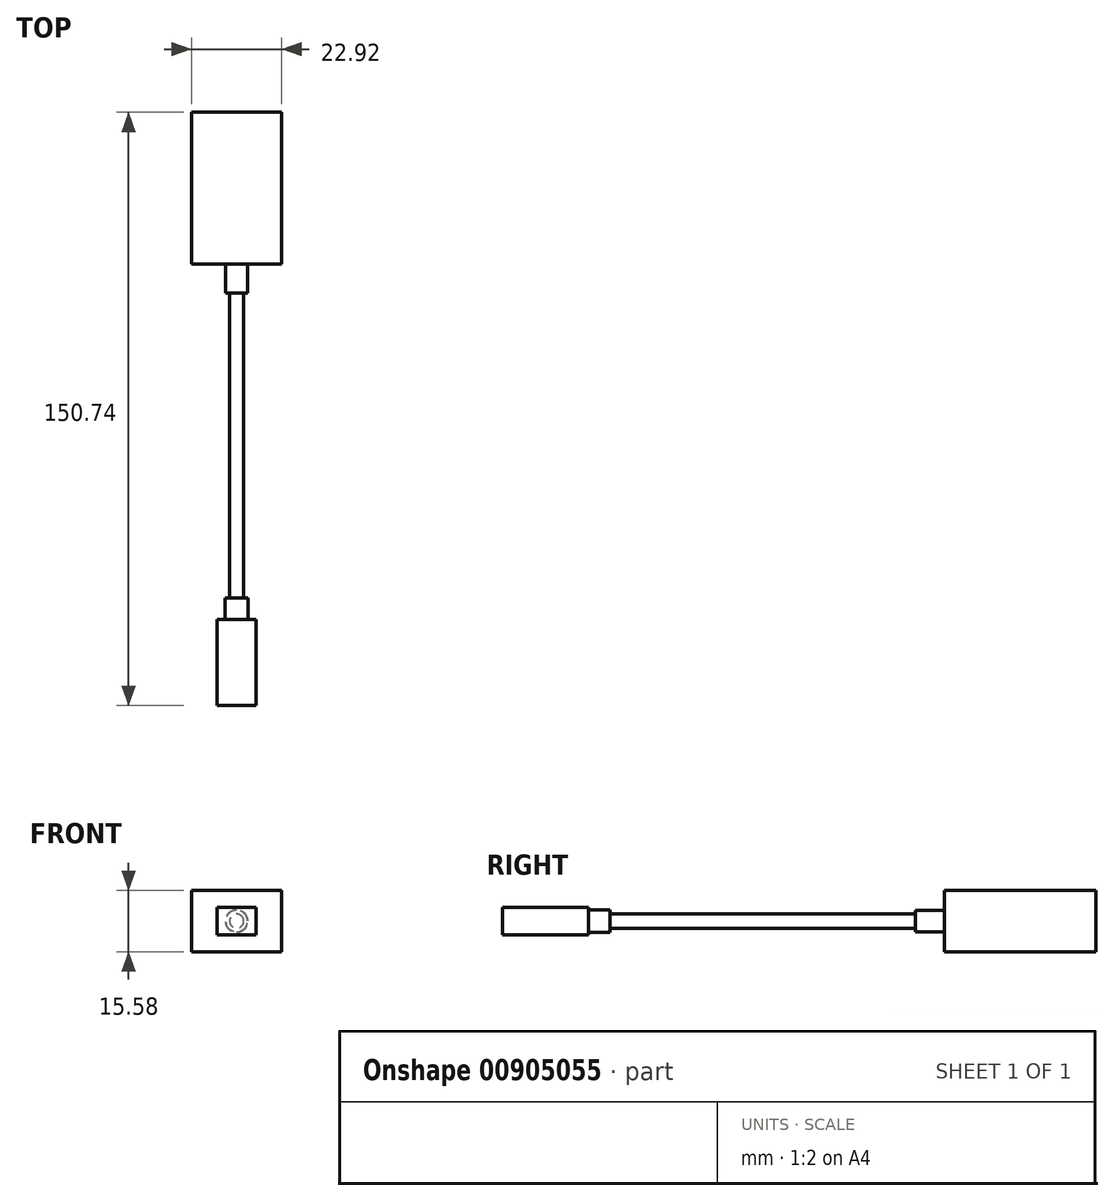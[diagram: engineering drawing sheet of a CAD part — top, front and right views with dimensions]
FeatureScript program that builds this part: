
annotation { "Feature Type Name" : "Feature", "Feature Type Description" : "" }
export const myFeature = defineFeature(function(context is Context, id is Id, definition is map)
    precondition{}
    {
        {
            var Q0;
            Q0=qCreatedBy(makeId("Top.planeOp"),FACE);
            var sketch = newSketch(context, id + "F0", { "sketchPlane" : qUnion([Q0])});
            skLineSegment(sketch, "E0.bottom", {"start": v(4.94, -10.92) * mm, "end": v(-4.94, -10.92) * mm});
            skLineSegment(sketch, "E0.top", {"start": v(4.94, 10.92) * mm, "end": v(-4.94, 10.92) * mm});
            skLineSegment(sketch, "E0.left", {"start": v(4.94, -10.92) * mm, "end": v(4.94, 10.92) * mm});
            skLineSegment(sketch, "E0.right", {"start": v(-4.94, -10.92) * mm, "end": v(-4.94, 10.92) * mm});
            skPoint(sketch, "E0.middle", {"position": v(0, 0) * mm});
            skLineSegment(sketch, "E1.bottom", {"start": v(-2.87, 10.92) * mm, "end": v(2.88, 10.92) * mm});
            skLineSegment(sketch, "E1.top", {"start": v(-2.87, 16.42) * mm, "end": v(2.88, 16.42) * mm});
            skLineSegment(sketch, "E1.left", {"start": v(-2.87, 10.92) * mm, "end": v(-2.87, 16.42) * mm});
            skLineSegment(sketch, "E1.right", {"start": v(2.88, 10.92) * mm, "end": v(2.88, 16.42) * mm});
            skLineSegment(sketch, "E2.bottom", {"start": v(-1.8, 16.42) * mm, "end": v(1.8, 16.42) * mm});
            skLineSegment(sketch, "E2.top", {"start": v(-1.8, 93.92) * mm, "end": v(1.8, 93.92) * mm});
            skLineSegment(sketch, "E2.left", {"start": v(-1.8, 16.42) * mm, "end": v(-1.8, 93.92) * mm});
            skLineSegment(sketch, "E2.right", {"start": v(1.8, 16.42) * mm, "end": v(1.8, 93.92) * mm});
            skLineSegment(sketch, "E3.bottom", {"start": v(-2.75, 93.92) * mm, "end": v(2.75, 93.92) * mm});
            skLineSegment(sketch, "E3.top", {"start": v(-2.75, 101.27) * mm, "end": v(2.75, 101.27) * mm});
            skLineSegment(sketch, "E3.left", {"start": v(-2.75, 93.92) * mm, "end": v(-2.75, 101.27) * mm});
            skLineSegment(sketch, "E3.right", {"start": v(2.75, 93.92) * mm, "end": v(2.75, 101.27) * mm});
            skLineSegment(sketch, "E4.bottom", {"start": v(-11.46, 101.27) * mm, "end": v(11.46, 101.27) * mm});
            skLineSegment(sketch, "E4.top", {"start": v(-11.46, 139.82) * mm, "end": v(11.46, 139.82) * mm});
            skLineSegment(sketch, "E4.left", {"start": v(-11.46, 101.27) * mm, "end": v(-11.46, 139.82) * mm});
            skLineSegment(sketch, "E4.right", {"start": v(11.46, 101.27) * mm, "end": v(11.46, 139.82) * mm});
            skSolve(sketch);
        }
        {
            var Q0;
            Q0=makeQuery(id+"F0.imprint","IMPRINT",FACE,{"disambiguationData":[TD([[makeQuery(id+"F0.imprint","IMPRINT",EDGE,{"derivedFrom":sQuery(id+"F0.wireOp",EDGE,"E4.top")}),-1.0]])]});
            extrude(context, id + "F1", {"entities" : qUnion([Q0]), "endBound" : BoundingType.SYMMETRIC, "depth" : 15.58 * mm, "offsetDistance" : 25 * mm});
        }
        {
            var Q0;
            Q0=makeQuery(id+"F0.imprint","IMPRINT",FACE,{"disambiguationData":[TD([[makeQuery(id+"F0.imprint","IMPRINT",EDGE,{"derivedFrom":sQuery(id+"F0.wireOp",EDGE,"E0.bottom")}),-1.0]])]});
            extrude(context, id + "F2", {"entities" : qUnion([Q0]), "endBound" : BoundingType.SYMMETRIC, "depth" : 6.92 * mm, "offsetDistance" : 25 * mm});
        }
        {
            var Q0;
            Q0=makeQuery(id+"F2.opExtrude","SWEPT_FACE",FACE,{"disambiguationData":[OSD([sQuery(id+"F0.wireOp",EDGE,"E0.top"),sQuery(id+"F0.wireOp",EDGE,"E1.bottom")])]});
            var sketch = newSketch(context, id + "F3", { "sketchPlane" : qUnion([Q0])});
            skCircle(sketch, "E5", {"center": v(0, 0) * mm, "radius": 2.88 * mm});
            skPoint(sketch, "E5.centerSnap0", {"position": v(0, -3.46) * mm});
            skPoint(sketch, "E5.centerSnap1", {"position": v(-4.94, 0) * mm});
            skSolve(sketch);
        }
        {
            var Q0;
            Q0=makeQuery(id+"F3.imprint","IMPRINT",FACE,{"disambiguationData":[TD([[makeQuery(id+"F3.imprint","IMPRINT",EDGE,{"derivedFrom":sQuery(id+"F3.wireOp",EDGE,"E5")}),1.0]])]});
            var Q1;
            Q1=sQuery(id+"F0.wireOp",VERTEX,"E1.top.end");
            extrude(context, id + "F4", {"entities" : qUnion([Q0]), "operationType" : NewBodyOperationType.ADD, "endBound" : BoundingType.UP_TO_VERTEX, "depth" : 25 * mm, "endBoundEntityVertex" : qUnion([Q1]), "offsetDistance" : 25 * mm});
        }
        {
            var Q0;
            Q0=makeQuery(id+"F4.opExtrude","CAP_FACE",FACE,{"disambiguationData":[OSD([sQuery(id+"F3.wireOp",EDGE,"E5")])],"isStart":false});
            var sketch = newSketch(context, id + "F5", { "sketchPlane" : qUnion([Q0])});
            skCircle(sketch, "E6", {"center": v(0, 0) * mm, "radius": 1.8 * mm});
            skSolve(sketch);
        }
        {
            var Q0;
            Q0=makeQuery(id+"F5.imprint","IMPRINT",FACE,{"disambiguationData":[TD([[makeQuery(id+"F5.imprint","IMPRINT",EDGE,{"derivedFrom":sQuery(id+"F5.wireOp",EDGE,"E6")}),1.0]])]});
            var Q1;
            Q1=sQuery(id+"F0.wireOp",EDGE,"E2.right");
            sweep(context, id + "F6", {"operationType" : NewBodyOperationType.ADD, "profiles" : qUnion([Q0]), "path" : qUnion([Q1])});
        }
        {
            var Q0;
            Q0=makeQuery(id+"F1.opExtrude","SWEPT_FACE",FACE,{"disambiguationData":[OSD([sQuery(id+"F0.wireOp",EDGE,"E4.bottom")])]});
            var sketch = newSketch(context, id + "F7", { "sketchPlane" : qUnion([Q0])});
            skCircle(sketch, "E7", {"center": v(0, 0) * mm, "radius": 2.75 * mm});
            skSolve(sketch);
        }
        {
            var Q0;
            Q0 = qSketchRegion(id + "F7", true);
            var Q1;
            Q1=makeQuery(id+"F6.opSweep","CAP_FACE",FACE,{"disambiguationData":[OSD([sQuery(id+"F0.wireOp",VERTEX,"E2.right.end"),sQuery(id+"F5.wireOp",EDGE,"E6")])],"isStart":false});
            extrude(context, id + "F8", {"entities" : qUnion([Q0]), "operationType" : NewBodyOperationType.ADD, "endBound" : BoundingType.UP_TO_SURFACE, "depth" : 25 * mm, "endBoundEntityFace" : qUnion([Q1]), "offsetDistance" : 25 * mm});
        }
    });
